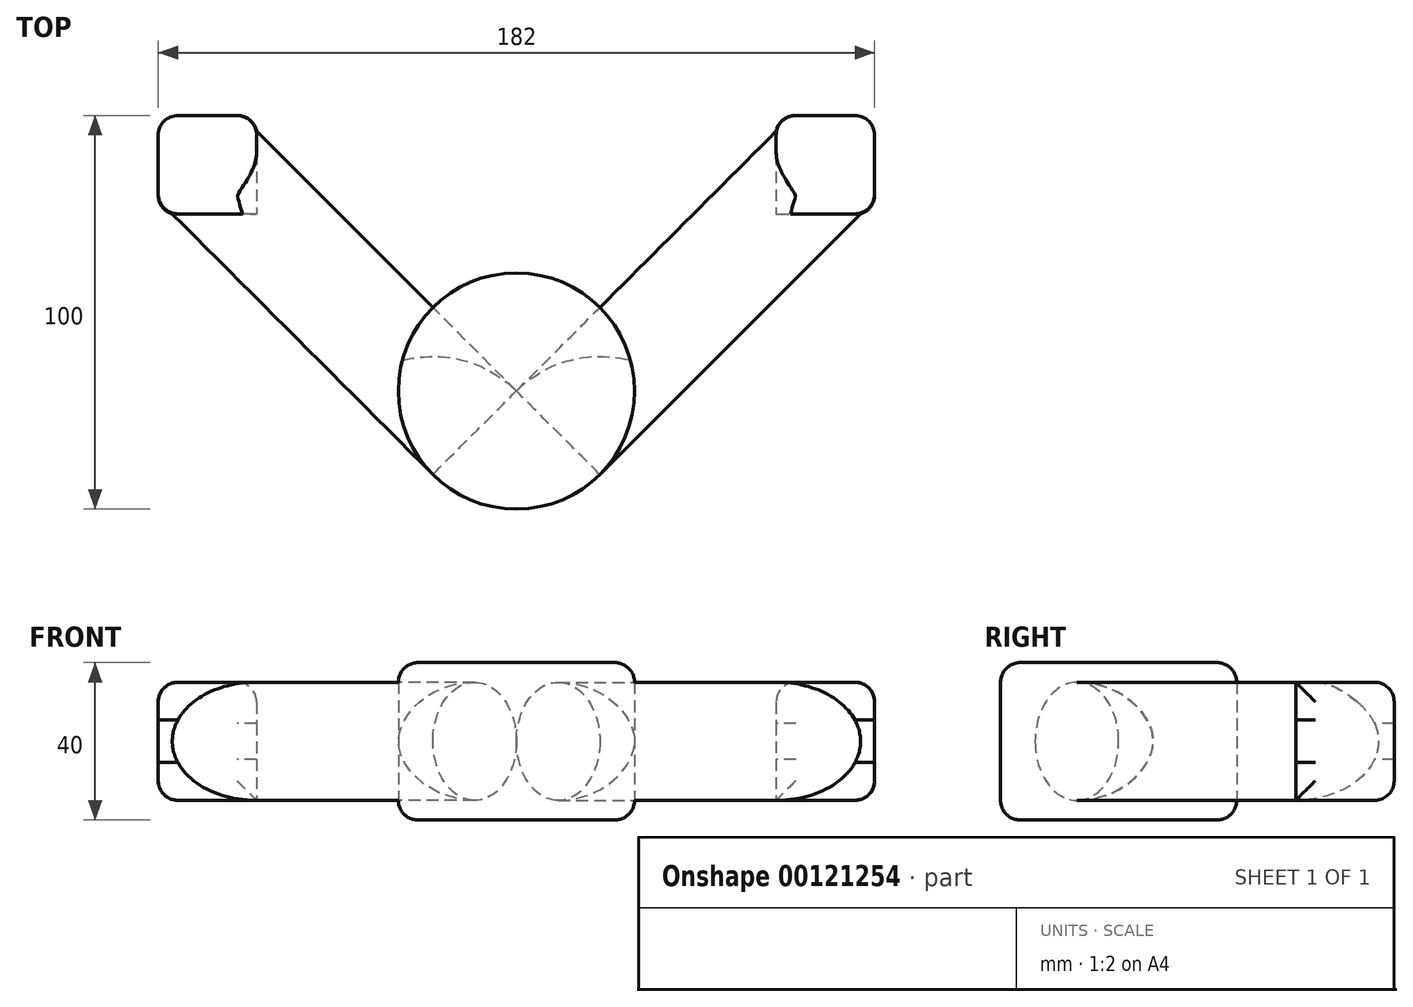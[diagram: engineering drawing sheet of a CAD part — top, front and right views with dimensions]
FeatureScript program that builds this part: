
annotation { "Feature Type Name" : "Feature", "Feature Type Description" : "" }
export const myFeature = defineFeature(function(context is Context, id is Id, definition is map)
    precondition{}
    {
        {
            var Q0;
            Q0=qCreatedBy(makeId("Top.planeOp"),FACE);
            var sketch = newSketch(context, id + "F0", { "sketchPlane" : qUnion([Q0])});
            skCircle(sketch, "E0", {"center": v(0, 0) * mm, "radius": 30 * mm});
            skLineSegment(sketch, "E1", {"start": v(0, 0) * mm, "end": v(-70.71, 70.71) * mm});
            skLineSegment(sketch, "E2", {"start": v(-21.21, -21.21) * mm, "end": v(-91.92, 49.5) * mm});
            skLineSegment(sketch, "E3.MirrorCS", {"start": v(0, 0) * mm, "end": v(70.71, 70.71) * mm});
            skLineSegment(sketch, "E4.MirrorCS", {"start": v(21.21, -21.21) * mm, "end": v(91.92, 49.5) * mm});
            skLineSegment(sketch, "E5", {"start": v(-70.71, 70.71) * mm, "end": v(-91.92, 49.5) * mm});
            skLineSegment(sketch, "E6.MirrorCS", {"start": v(70.71, 70.71) * mm, "end": v(91.92, 49.5) * mm});
            skPoint(sketch, "E7", {"position": v(-81.32, 60.1) * mm});
            skLineSegment(sketch, "E8", {"start": v(-81.32, 60.1) * mm, "end": v(0, -21.21) * mm});
            skLineSegment(sketch, "E9.MirrorCS", {"start": v(81.32, 60.1) * mm, "end": v(0, -21.21) * mm});
            skSolve(sketch);
        }
        {
            var Q0;
            {var subQ0=sQuery(id+"F0.wireOp",EDGE,"E2");Q0=makeQuery(id+"F0.imprint","IMPRINT",FACE,{"disambiguationData":[TD([[makeQuery(id+"F0.imprint","IMPRINT",EDGE,{"derivedFrom":subQ0}),-1.0]])]});}
            var Q1;
            Q1=sQuery(id+"F0.wireOp",EDGE,"E8");
            revolve(context, id + "F1", {"entities" : qUnion([Q0]), "axis" : qUnion([Q1]), "revolveType" : RevolveType.FULL});
        }
        {
            var Q0;
            {var subQ0=sQuery(id+"F0.wireOp",EDGE,"E4.MirrorCS");Q0=makeQuery(id+"F0.imprint","IMPRINT",FACE,{"disambiguationData":[TD([[makeQuery(id+"F0.imprint","IMPRINT",EDGE,{"derivedFrom":subQ0}),1.0]])]});}
            var Q1;
            Q1=sQuery(id+"F0.wireOp",EDGE,"E9.MirrorCS");
            revolve(context, id + "F2", {"entities" : qUnion([Q0]), "axis" : qUnion([Q1]), "revolveType" : RevolveType.FULL});
        }
        {
            var Q0;
            {var subQ0=sQuery(id+"F0.wireOp",EDGE,"E3.MirrorCS");var subQ1=sQuery(id+"F0.wireOp",EDGE,"E0");var subQ2=makeQuery(id+"F0.imprint","INTERSECT",VERTEX,{"derivedFrom":[subQ1,subQ0]});Q0=makeQuery(id+"F0.imprint","IMPRINT",FACE,{"disambiguationData":[TD([[makeQuery(id+"F0.imprint","IMPRINT",EDGE,{"disambiguationData":[TD([[subQ2,-1.0]])],"derivedFrom":subQ1}),1.0]])]});}
            var Q1;
            {var subQ0=sQuery(id+"F0.wireOp",EDGE,"E3.MirrorCS");var subQ3=sQuery(id+"F0.wireOp",EDGE,"E0");var subQ4=makeQuery(id+"F0.imprint","INTERSECT",VERTEX,{"derivedFrom":[subQ3,subQ0]});Q1=makeQuery(id+"F0.imprint","IMPRINT",FACE,{"disambiguationData":[TD([[makeQuery(id+"F0.imprint","IMPRINT",EDGE,{"disambiguationData":[TD([[subQ4,1.0]])],"derivedFrom":subQ3}),1.0]])]});}
            var Q2;
            {var subQ0=sQuery(id+"F0.wireOp",EDGE,"E0");var subQ4=makeQuery(id+"F0.imprint","INTERSECT",VERTEX,{"derivedFrom":[subQ0,sQuery(id+"F0.wireOp",EDGE,"E2")]});Q2=makeQuery(id+"F0.imprint","IMPRINT",FACE,{"disambiguationData":[TD([[makeQuery(id+"F0.imprint","IMPRINT",EDGE,{"disambiguationData":[TD([[subQ4,1.0]])],"derivedFrom":subQ0}),1.0]])]});}
            extrude(context, id + "F3", {"entities" : qUnion([Q0, Q1, Q2]), "endBound" : BoundingType.SYMMETRIC, "depth" : 40 * mm});
        }
        {
            var Q0;
            Q0=makeQuery(id+"F3.opExtrude","CAP_FACE",FACE,{"disambiguationData":[OSD([sQuery(id+"F0.wireOp",EDGE,"E0")])],"isStart":false});
            var Q1;
            Q1=makeQuery(id+"F3.opExtrude","CAP_FACE",FACE,{"disambiguationData":[OSD([sQuery(id+"F0.wireOp",EDGE,"E0")])],"isStart":true});
            var Q2;
            Q2=makeQuery(id+"F1.opRevolve","SWEPT_FACE",FACE,{"disambiguationData":[OSD([sQuery(id+"F0.wireOp",EDGE,"E5")])]});
            var Q3;
            Q3=makeQuery(id+"F2.opRevolve","SWEPT_FACE",FACE,{"disambiguationData":[OSD([sQuery(id+"F0.wireOp",EDGE,"E6.MirrorCS")])]});
            fillet(context, id + "F4", {"entities" : qUnion([Q0, Q1, Q2, Q3]), "radius" : 5 * mm, "tangentPropagation" : true, "allowEdgeOverflow" : false});
        }
        {
            var Q0;
            Q0=qCreatedBy(makeId("Front.planeOp"),FACE);
            cPlane(context, id + "F5", {"entities" : qUnion([Q0]), "cplaneType" : CPlaneType.OFFSET, "offset" : 45 * mm, "oppositeDirection" : true, "width" : 150 * mm, "height" : 150 * mm});
        }
        {
            var Q0;
            Q0=qCreatedBy(id+"F5.planeOp",FACE);
            var sketch = newSketch(context, id + "F6", { "sketchPlane" : qUnion([Q0])});
            skLineSegment(sketch, "E10", {"start": v(0, 0) * mm, "end": v(0, 40.64) * mm});
            skLineSegment(sketch, "E11", {"start": v(66, 0) * mm, "end": v(-66, 0) * mm});
            skLineSegment(sketch, "E12.bottom", {"start": v(66, 15) * mm, "end": v(91, 15) * mm});
            skLineSegment(sketch, "E12.top", {"start": v(66, -15) * mm, "end": v(91, -15) * mm});
            skLineSegment(sketch, "E12.left", {"start": v(66, 15) * mm, "end": v(66, -15) * mm});
            skLineSegment(sketch, "E12.right", {"start": v(91, 15) * mm, "end": v(91, -15) * mm});
            skLineSegment(sketch, "E13.MirrorCS", {"start": v(-66, 15) * mm, "end": v(-91, 15) * mm});
            skLineSegment(sketch, "E14.MirrorCS", {"start": v(-66, 15) * mm, "end": v(-66, -15) * mm});
            skLineSegment(sketch, "E15.MirrorCS", {"start": v(-66, -15) * mm, "end": v(-91, -15) * mm});
            skLineSegment(sketch, "E16.MirrorCS", {"start": v(-91, 15) * mm, "end": v(-91, -15) * mm});
            skSolve(sketch);
        }
        {
            var Q0;
            {var subQ3=sQuery(id+"F6.wireOp",EDGE,"E12.bottom");Q0=makeQuery(id+"F6.imprint","IMPRINT",FACE,{"disambiguationData":[TD([[makeQuery(id+"F6.imprint","IMPRINT",EDGE,{"derivedFrom":subQ3}),-1.0]])]});}
            var Q1;
            {var subQ3=sQuery(id+"F6.wireOp",EDGE,"E13.MirrorCS");Q1=makeQuery(id+"F6.imprint","IMPRINT",FACE,{"disambiguationData":[TD([[makeQuery(id+"F6.imprint","IMPRINT",EDGE,{"derivedFrom":subQ3}),1.0]])]});}
            extrude(context, id + "F7", {"entities" : qUnion([Q0, Q1]), "operationType" : NewBodyOperationType.ADD, "oppositeDirection" : true, "depth" : 25 * mm});
        }
        {
            var Q0;
            Q0=makeQuery(id+"F7.opExtrude","CAP_FACE",FACE,{"disambiguationData":[OSD([sQuery(id+"F6.wireOp",EDGE,"E12.bottom"),sQuery(id+"F6.wireOp",EDGE,"E12.top"),sQuery(id+"F6.wireOp",EDGE,"E12.left"),sQuery(id+"F6.wireOp",EDGE,"E12.right")])],"isStart":false});
            var Q1;
            Q1=makeQuery(id+"F7.opExtrude","CAP_FACE",FACE,{"disambiguationData":[OSD([sQuery(id+"F6.wireOp",EDGE,"E13.MirrorCS"),sQuery(id+"F6.wireOp",EDGE,"E14.MirrorCS"),sQuery(id+"F6.wireOp",EDGE,"E15.MirrorCS"),sQuery(id+"F6.wireOp",EDGE,"E16.MirrorCS")])],"isStart":false});
            var Q2;
            Q2=makeQuery(id+"F7.opExtrude","SWEPT_FACE",FACE,{"disambiguationData":[OSD([sQuery(id+"F6.wireOp",EDGE,"E16.MirrorCS")])]});
            var Q3;
            Q3=makeQuery(id+"F7.opExtrude","SWEPT_FACE",FACE,{"disambiguationData":[OSD([sQuery(id+"F6.wireOp",EDGE,"E12.right")])]});
            var Q4;
            Q4=makeQuery(id+"F7.opExtrude","SWEPT_EDGE",EDGE,{"disambiguationData":[OSD([sQuery(id+"F6.wireOp",EDGE,"E13.MirrorCS"),sQuery(id+"F6.wireOp",EDGE,"E14.MirrorCS")])]});
            var Q5;
            Q5=makeQuery(id+"F7.opExtrude","SWEPT_EDGE",EDGE,{"disambiguationData":[OSD([sQuery(id+"F6.wireOp",EDGE,"E12.bottom"),sQuery(id+"F6.wireOp",EDGE,"E12.left")])]});
            fillet(context, id + "F8", {"entities" : qUnion([Q0, Q1, Q2, Q3, Q4, Q5]), "radius" : 5 * mm, "tangentPropagation" : true, "allowEdgeOverflow" : false});
        }
    });
